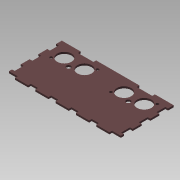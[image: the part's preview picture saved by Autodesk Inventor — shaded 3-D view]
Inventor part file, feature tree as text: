
AUTODESK INVENTOR PART (.ipt)
format: ipt  version: 2015 SP1 (Build 190203100, 203)  size: 172,032 bytes
history: native  units: mm
features: extrude x1, sketch x1
ambient origin geometry x8: Origin, YZ Plane, XZ Plane, XY Plane, X Axis, Y Axis, Z Axis, Center Point
bodies: Solid1 (feature_tree)
feature tree (2):
  extrude  "Extrusion1"  Depth=3.0mm
  sketch  "Sketch1"  dims[d0=15.0mm d1=3.0mm d3=30.0mm d5=23.0mm d6=30.0mm d8=23.0mm d11=3.0mm d12=3.0mm d13=90.0deg d14=3.0mm d17=3.0mm d18=10.0mm d20=10.0mm d21=2.0mm d22=0.0mm]
